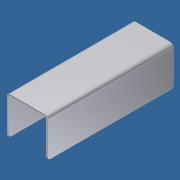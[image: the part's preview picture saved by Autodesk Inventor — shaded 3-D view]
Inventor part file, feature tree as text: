
AUTODESK INVENTOR PART (.ipt)
format: ipt  version: 2012 (Build 160160000, 160)  size: 92,160 bytes
history: native  units: in
note: dims shown in document units (in); Inventor stores cm internally (conversion verified against a paired STEP export)
features: other x3, sketch x1
ambient origin geometry x8: Origin, YZ Plane, XZ Plane, XY Plane, X Axis, Y Axis, Z Axis, Center Point
bodies: Solid1 (feature_tree)
feature tree (4):
  other  "GE-12052.ipt"
  other  "Solid1::GE-12052.ipt"
  sketch  "Sketch1"  dims[d0=0.3937in]
  other  "TaggingFeature1"
